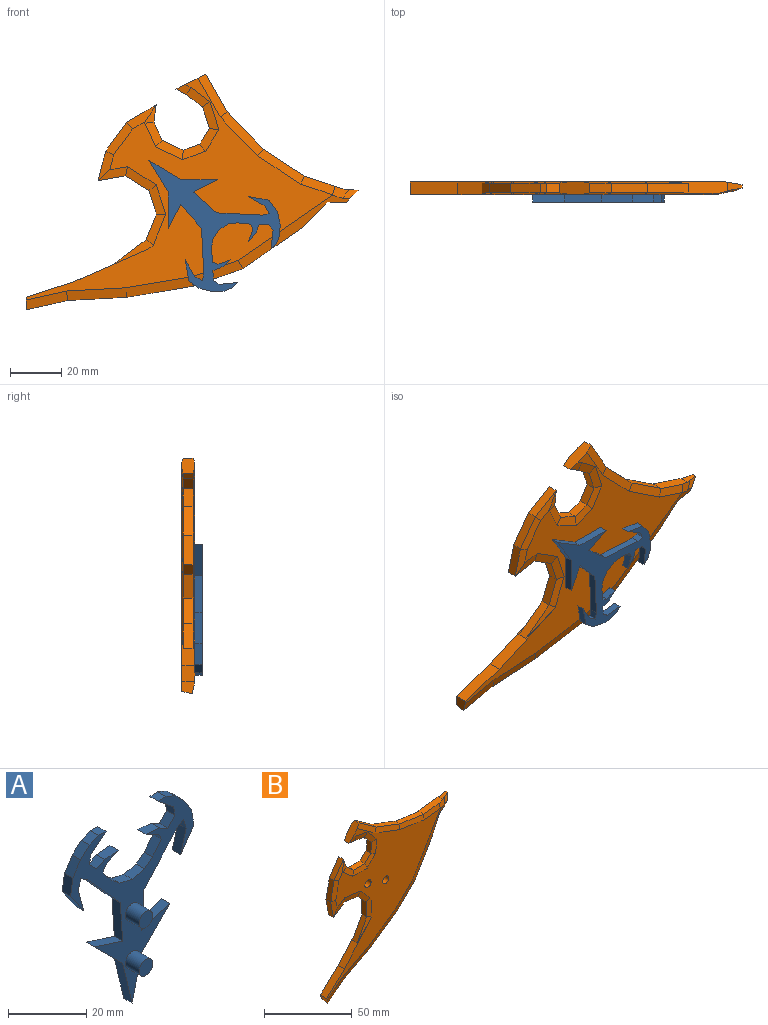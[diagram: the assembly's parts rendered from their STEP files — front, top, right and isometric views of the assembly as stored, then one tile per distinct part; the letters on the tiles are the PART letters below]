
ASSEMBLY  parts=2 mates=1
PART A: 54 faces, bbox 44.5x8x58.5 mm
  f0: plane 4.86x3mm, normal (0.09,0,1), area 14.7mm2, adj f1,f47,f48,f49
  f1: plane 4.63x3mm, normal (-0.45,0,-0.89), area 15.5mm2, adj f0,f2,f48,f49
  f2: plane 3x1.97mm, normal (-0.9,0,-0.43), area 6.5mm2, adj f1,f3,f48,f49
  f3: plane 3.99x3.27mm, normal (-0.77,0,0.63), area 15.5mm2, adj f2,f4,f48,f49
  f4: plane 3x2.86mm, normal (-0.62,0,0.79), area 10.9mm2, adj f3,f5,f48,f49
  f5: plane 4.44x3mm, normal (-0.23,0,0.97), area 13.7mm2, adj f4,f6,f48,f49
  f6: plane 4.44x3mm, normal (0.23,0,0.97), area 13.7mm2, adj f5,f7,f48,f49
  f7: plane 3x2.86mm, normal (0.62,0,0.79), area 10.9mm2, adj f6,f8,f48,f49
  f8: plane 3.99x3.27mm, normal (0.77,0,0.63), area 15.5mm2, adj f7,f9,f48,f49
  f9: plane 3x1.97mm, normal (0.9,0,-0.43), area 6.5mm2, adj f8,f10,f48,f49
  f10: plane 4.63x3mm, normal (0.45,0,-0.89), area 15.5mm2, adj f9,f11,f48,f49
  f11: plane 4.86x3mm, normal (-0.09,0,1), area 14.7mm2, adj f10,f12,f48,f49
  f12: plane 3x2.89mm, normal (-0.46,0,0.89), area 9.8mm2, adj f11,f13,f48,f49
  f13: plane 3x2.78mm, normal (0.72,0,0.69), area 11.5mm2, adj f12,f14,f48,f49
  f14: plane 3x2.78mm, normal (0.99,0,-0.16), area 8.5mm2, adj f13,f15,f48,f49
  f15: plane 5.56x4.52mm, normal (0.63,0,-0.78), area 21.5mm2, adj f14,f16,f48,f49
  f16: plane 3x2.78mm, normal (0.04,0,1), area 8.3mm2, adj f15,f17,f48,f49
  f17: plane 3.24x3mm, normal (-0.39,0,0.92), area 10.6mm2, adj f16,f18,f48,f49
  f18: plane 3.24x3.01mm, normal (-0.68,0,0.73), area 13.3mm2, adj f17,f19,f48,f49
  f19: plane 4.28x3mm, normal (-0.84,0,0.54), area 15.3mm2, adj f18,f20,f48,f49
  f20: plane 5.33x3mm, normal (-0.99,0,0.15), area 16.2mm2, adj f19,f21,f48,f49
  f21: plane 6.83x4.75mm, normal (-0.82,0,-0.57), area 25mm2, adj f20,f22,f48,f49
  f22: plane 7.29x3mm, normal (0.97,0,0.26), area 22.7mm2, adj f21,f23,f48,f49
  f23: plane 3.24x3mm, normal (0.96,0,-0.27), area 10.1mm2, adj f22,f24,f48,f49
  f24: plane 3x2.32mm, normal (-0.54,0,-0.84), area 8.3mm2, adj f23,f25,f48,f49
  f25: plane 13.22x11.97mm, normal (-0.74,0,-0.67), area 53.5mm2, adj f24,f26,f48,f49
  f26: plane 12.39x3mm, normal (-1,0,-0.07), area 37.3mm2, adj f25,f27,f48,f49
  f27: plane 10.19x3.3mm, normal (0.31,0,0.95), area 32.1mm2, adj f26,f28,f48,f49
  f28: plane 10.26x10.19mm, normal (-0.71,0,-0.7), area 43.4mm2, adj f27,f29,f48,f49
  f29: plane 14.11x3.44mm, normal (-0.97,0,-0.24), area 43.6mm2, adj f28,f30,f48,f49
  f30: plane 14.11x3.44mm, normal (0.97,0,-0.24), area 43.6mm2, adj f29,f31,f48,f49
  f31: plane 10.26x10.19mm, normal (0.71,0,-0.7), area 43.4mm2, adj f30,f32,f48,f49
  f32: plane 10.19x3.3mm, normal (-0.31,0,0.95), area 32.1mm2, adj f31,f33,f48,f49
  f33: plane 12.39x3mm, normal (1,0,-0.07), area 37.3mm2, adj f32,f34,f48,f49
  f34: plane 13.22x11.97mm, normal (0.74,0,-0.67), area 53.5mm2, adj f33,f35,f48,f49
  f35: plane 3x2.32mm, normal (0.54,0,-0.84), area 8.3mm2, adj f34,f36,f48,f49
  f36: plane 3.24x3mm, normal (-0.96,0,-0.27), area 10.1mm2, adj f35,f37,f48,f49
  f37: plane 7.29x3mm, normal (-0.97,0,0.26), area 22.7mm2, adj f36,f38,f48,f49
  f38: plane 6.83x4.75mm, normal (0.82,0,-0.57), area 25mm2, adj f37,f39,f48,f49
  f39: plane 5.33x3mm, normal (0.99,0,0.15), area 16.2mm2, adj f38,f40,f48,f49
  f40: plane 4.28x3mm, normal (0.84,0,0.54), area 15.3mm2, adj f39,f41,f48,f49
  f41: plane 3.24x3.01mm, normal (0.68,0,0.73), area 13.3mm2, adj f40,f42,f48,f49
  f42: plane 3.24x3mm, normal (0.39,0,0.92), area 10.6mm2, adj f41,f43,f48,f49
  f43: plane 3x2.78mm, normal (-0.04,0,1), area 8.3mm2, adj f42,f44,f48,f49
  f44: plane 5.56x4.52mm, normal (-0.63,0,-0.78), area 21.5mm2, adj f43,f45,f48,f49
  f45: plane 3x2.78mm, normal (-0.99,0,-0.16), area 8.5mm2, adj f44,f46,f48,f49
  f46: plane 3x2.78mm, normal (-0.72,0,0.69), area 11.5mm2, adj f45,f47,f48,f49
  f47: plane 3x2.89mm, normal (0.46,0,0.89), area 9.8mm2, adj f0,f46,f48,f49
  f48: plane 58.49x44.52mm, normal (0,-1,0), area 560.9mm2, adj f0,f1,f2,f3,f4,f5,f6,f7
  f49: plane 58.49x44.52mm, normal (0,1,0), area 600.1mm2, adj f0,f1,f2,f3,f4,f5,f6,f7
  f50: cylinder r=2.5mm len=5mm, axis (0,1,0), area 78.5mm2, adj f48,f51
  f51: plane 5x5mm, normal (0,-1,0), area 19.6mm2, adj f50
  f52: cylinder r=2.5mm len=5mm, axis (0,1,0), area 78.5mm2, adj f48,f53
  f53: plane 5x5mm, normal (0,-1,0), area 19.6mm2, adj f52
PART B: 88 faces, bbox 100.1x5x113.5 mm
  f0: plane 14.33x13.41mm, normal (-0.68,0,0.73), area 98.1mm2, adj f1,f32,f33,f34
  f1: plane 5x4.51mm, normal (-0.92,0,-0.4), area 20.7mm2, adj f0,f2,f33,f34,f41,f46
  f2: plane 13.29x10.22mm, normal (0.61,0,-0.79), area 4.5mm2, adj f1,f3,f41,f46
  f3: plane 20.44x10.9mm, normal (0.47,0,-0.88), area 6.2mm2, adj f2,f4,f40,f45
  f4: plane 21.81x14.99mm, normal (0.57,0,-0.82), area 7.1mm2, adj f3,f5,f39,f44
  f5: plane 14.65x14.31mm, normal (0.7,0,-0.72), area 5.5mm2, adj f4,f6,f38,f43
  f6: plane 24.53x14.31mm, normal (0.86,0,-0.5), area 81.4mm2, adj f5,f7,f37,f38,f42
  f7: plane 13.29x4.77mm, normal (0.94,0,-0.34), area 52.1mm2, adj f6,f8,f37,f42
  f8: plane 6.81x4.38mm, normal (0.41,0,-0.91), area 24mm2, adj f7,f9,f37,f42
  f9: plane 6.13x2.51mm, normal (0.95,0,-0.32), area 12.5mm2, adj f8,f10,f37,f42,f51
  f10: plane 5.18x3.27mm, normal (-0.37,0,0.93), area 13.1mm2, adj f9,f11,f37,f51
  f11: plane 30.79x4.4mm, normal (-0.12,0,0.99), area 74.4mm2, adj f10,f12,f34,f37,f50,f51,f52,f71
  f12: plane 19.07x3.8mm, normal (0.15,0,0.99), area 73.3mm2, adj f11,f13,f49,f71
  f13: plane 19.07x7.31mm, normal (0.36,0,0.93), area 77.6mm2, adj f12,f14,f48,f70
  f14: plane 13.72x9.78mm, normal (0.58,0,0.81), area 64mm2, adj f13,f15,f47,f69
  f15: plane 10.22x8.18mm, normal (-0.78,0,0.62), area 60.9mm2, adj f14,f16,f33,f34,f47,f67,f69,f87
  f16: plane 4.77x3.8mm, normal (-0.07,0,-1), area 18.2mm2, adj f15,f17,f67,f87
  f17: plane 7.64x3.8mm, normal (-0.2,0,-0.98), area 29.6mm2, adj f16,f18,f68,f86
  f18: plane 6.57x6.02mm, normal (-0.74,0,-0.68), area 33.9mm2, adj f17,f19,f66,f85
  f19: plane 7.12x3.8mm, normal (-0.99,0,0.11), area 27.2mm2, adj f18,f20,f65,f84
  f20: plane 4.93x4.93mm, normal (-0.71,0,0.71), area 26.5mm2, adj f19,f21,f64,f83
  f21: plane 9.03x3.8mm, normal (0,0,1), area 34.3mm2, adj f20,f22,f63,f82
  f22: plane 6.02x5.2mm, normal (0.65,0,0.76), area 30.2mm2, adj f21,f23,f62,f81
  f23: plane 6.47x3.8mm, normal (0.95,0,0.3), area 25.8mm2, adj f22,f24,f61,f80
  f24: plane 11.12x7.52mm, normal (-0.83,0,0.56), area 51mm2, adj f23,f25,f60,f79
  f25: plane 13.68x3.8mm, normal (-0.98,0,0.2), area 53mm2, adj f24,f26,f59,f78
  f26: plane 11.77x3.8mm, normal (-0.98,0,-0.18), area 45.5mm2, adj f25,f27,f58,f77
  f27: plane 9.03x6.29mm, normal (0.57,0,-0.82), area 41.8mm2, adj f26,f28,f57,f76
  f28: plane 10.67x3.8mm, normal (-0.13,0,-0.99), area 40.9mm2, adj f27,f29,f56,f75
  f29: plane 7.12x6.57mm, normal (-0.73,0,-0.68), area 36.8mm2, adj f28,f30,f55,f74
  f30: plane 10.88x3.8mm, normal (-1,0,-0.05), area 41.4mm2, adj f29,f31,f54,f73
  f31: plane 14.2x7.63mm, normal (-0.88,0,0.47), area 61.2mm2, adj f30,f32,f53,f72
  f32: plane 24.05x21.04mm, normal (-0.75,0,0.66), area 93mm2, adj f0,f31,f33,f34,f53,f72
  f33: plane 107.27x91.79mm, normal (0,-1,0), area 2985.7mm2, adj f0,f1,f15,f32,f35,f36,f42,f43
  f34: plane 109.86x93.99mm, normal (0,1,0), area 3276.7mm2, adj f0,f1,f11,f15,f32,f35,f36,f37
  f35: cylinder r=2.5mm len=5mm, axis (0,-1,0), area 78.5mm2, adj f33,f34
  f36: cylinder r=2.5mm len=5mm, axis (0,-1,0), area 78.5mm2, adj f33,f34
  f37: plane 53.58x36.09mm, normal (0.22,0.97,-0.13), area 199.8mm2, adj f6,f7,f8,f9,f10,f11,f34,f38
  f38: plane 16.69x16.68mm, normal (0.67,0.26,-0.69), area 78.7mm2, adj f5,f6,f34,f37,f39
  f39: plane 22.33x15.77mm, normal (0.55,0.26,-0.8), area 102mm2, adj f4,f34,f38,f40
  f40: plane 20.99x11.76mm, normal (0.45,0.26,-0.85), area 89.6mm2, adj f3,f34,f39,f41
  f41: plane 13.7x11.07mm, normal (0.59,0.26,-0.77), area 64.4mm2, adj f1,f2,f34,f40
  f42: plane 42.66x29.46mm, normal (0.22,-0.97,-0.13), area 160.6mm2, adj f6,f7,f8,f9,f33,f43,f51,f52
  f43: plane 17.03x16.63mm, normal (0.18,-0.97,-0.19), area 77.5mm2, adj f5,f33,f42,f44
  f44: plane 23.75x17.89mm, normal (0.15,-0.97,-0.21), area 101.2mm2, adj f4,f33,f43,f45
  f45: plane 22.47x14.1mm, normal (0.12,-0.97,-0.23), area 89.7mm2, adj f3,f33,f44,f46
  f46: plane 14.81x13.37mm, normal (0.16,-0.97,-0.21), area 63.5mm2, adj f1,f2,f33,f45
  f47: plane 15.85x12.8mm, normal (0.1,-0.98,0.14), area 59.3mm2, adj f14,f15,f33,f48
  f48: plane 20.7x10.62mm, normal (0.06,-0.98,0.16), area 72mm2, adj f13,f33,f47,f49
  f49: plane 19.95x6.29mm, normal (0.03,-0.98,0.17), area 68.1mm2, adj f12,f33,f48,f50
  f50: plane 13.07x4.92mm, normal (-0.02,-0.98,0.17), area 44.8mm2, adj f11,f33,f49,f52
  f51: plane 5.44x5.18mm, normal (0.09,-0.97,0.21), area 12.3mm2, adj f9,f10,f11,f42,f52
  f52: plane 5.27x4.09mm, normal (0.19,-0.96,0.19), area 17.2mm2, adj f11,f33,f42,f50,f51
  f53: plane 14.2x11.07mm, normal (-0.15,-0.98,0.08), area 31.8mm2, adj f31,f32,f33,f54
  f54: plane 13.06x4.04mm, normal (-0.17,-0.98,-0.01), area 41.4mm2, adj f30,f33,f53,f55
  f55: plane 10.33x9.9mm, normal (-0.13,-0.98,-0.12), area 37.7mm2, adj f29,f33,f54,f56
  f56: plane 13.2x4.91mm, normal (-0.02,-0.98,-0.17), area 41.6mm2, adj f28,f33,f55,f57
  f57: plane 9.84x9.03mm, normal (0.1,-0.98,-0.14), area 31.2mm2, adj f27,f33,f56,f58
  f58: plane 11.77x4.57mm, normal (-0.17,-0.98,-0.03), area 31.1mm2, adj f26,f33,f57,f59
  f59: plane 13.71x5.94mm, normal (-0.17,-0.98,0.03), area 45.9mm2, adj f25,f33,f58,f60
  f60: plane 12.46x7.52mm, normal (-0.14,-0.98,0.1), area 33.1mm2, adj f24,f33,f59,f61
  f61: plane 8.42x3.17mm, normal (0.17,-0.98,0.05), area 13mm2, adj f23,f33,f60,f62
  f62: plane 8.97x8.6mm, normal (0.11,-0.98,0.13), area 31.3mm2, adj f22,f33,f61,f63
  f63: plane 11.71x3.4mm, normal (0,-0.98,0.17), area 35.8mm2, adj f21,f33,f62,f64
  f64: plane 8.33x8.17mm, normal (-0.12,-0.98,0.12), area 28.6mm2, adj f20,f33,f63,f65
  f65: plane 9.84x4.38mm, normal (-0.17,-0.98,0.02), area 29.5mm2, adj f19,f33,f64,f66
  f66: plane 9.68x9.58mm, normal (-0.13,-0.98,-0.12), area 35.4mm2, adj f18,f33,f65,f68
  f67: plane 5.24x3.57mm, normal (-0.01,-0.98,-0.17), area 12.9mm2, adj f15,f16,f33,f68
  f68: plane 9.4x4.96mm, normal (-0.04,-0.98,-0.17), area 29.2mm2, adj f17,f33,f66,f67
  f69: plane 15.85x12.8mm, normal (0.1,0.98,0.14), area 59.3mm2, adj f14,f15,f34,f70
  f70: plane 20.7x10.62mm, normal (0.06,0.98,0.16), area 72mm2, adj f13,f34,f69,f71
  f71: plane 19.95x4.37mm, normal (0.03,0.98,0.17), area 45.7mm2, adj f11,f12,f34,f70
  f72: plane 14.2x11.07mm, normal (-0.15,0.98,0.08), area 31.8mm2, adj f31,f32,f34,f73
  f73: plane 13.06x4.04mm, normal (-0.17,0.98,-0.01), area 41.4mm2, adj f30,f34,f72,f74
  f74: plane 10.33x9.9mm, normal (-0.13,0.98,-0.12), area 37.7mm2, adj f29,f34,f73,f75
  f75: plane 13.2x4.91mm, normal (-0.02,0.98,-0.17), area 41.6mm2, adj f28,f34,f74,f76
  f76: plane 9.84x9.03mm, normal (0.1,0.98,-0.14), area 31.2mm2, adj f27,f34,f75,f77
  f77: plane 11.77x4.57mm, normal (-0.17,0.98,-0.03), area 31.1mm2, adj f26,f34,f76,f78
  f78: plane 13.71x5.94mm, normal (-0.17,0.98,0.03), area 45.9mm2, adj f25,f34,f77,f79
  f79: plane 12.46x7.52mm, normal (-0.14,0.98,0.1), area 33.1mm2, adj f24,f34,f78,f80
  f80: plane 8.42x3.17mm, normal (0.17,0.98,0.05), area 13mm2, adj f23,f34,f79,f81
  f81: plane 8.97x8.6mm, normal (0.11,0.98,0.13), area 31.3mm2, adj f22,f34,f80,f82
  f82: plane 11.71x3.4mm, normal (0,0.98,0.17), area 35.8mm2, adj f21,f34,f81,f83
  f83: plane 8.33x8.17mm, normal (-0.12,0.98,0.12), area 28.6mm2, adj f20,f34,f82,f84
  f84: plane 9.84x4.38mm, normal (-0.17,0.98,0.02), area 29.5mm2, adj f19,f34,f83,f85
  f85: plane 9.68x9.58mm, normal (-0.13,0.98,-0.12), area 35.4mm2, adj f18,f34,f84,f86
  f86: plane 9.4x4.96mm, normal (-0.04,0.98,-0.17), area 29.2mm2, adj f17,f34,f85,f87
  f87: plane 5.24x3.57mm, normal (-0.01,0.98,-0.17), area 12.9mm2, adj f15,f16,f34,f86
PLACE A rot(axis=(0.92,0,0.38),180deg) t=(11.94,-6.02,75.64)mm
PLACE B rot(axis=(0,1,0),25deg) t=(-36.07,1.98,21.93)mm
MATE revolute B.f36 <-> A.f50  axis (0,1,0) through (32.18,1.98,55.4)mm
